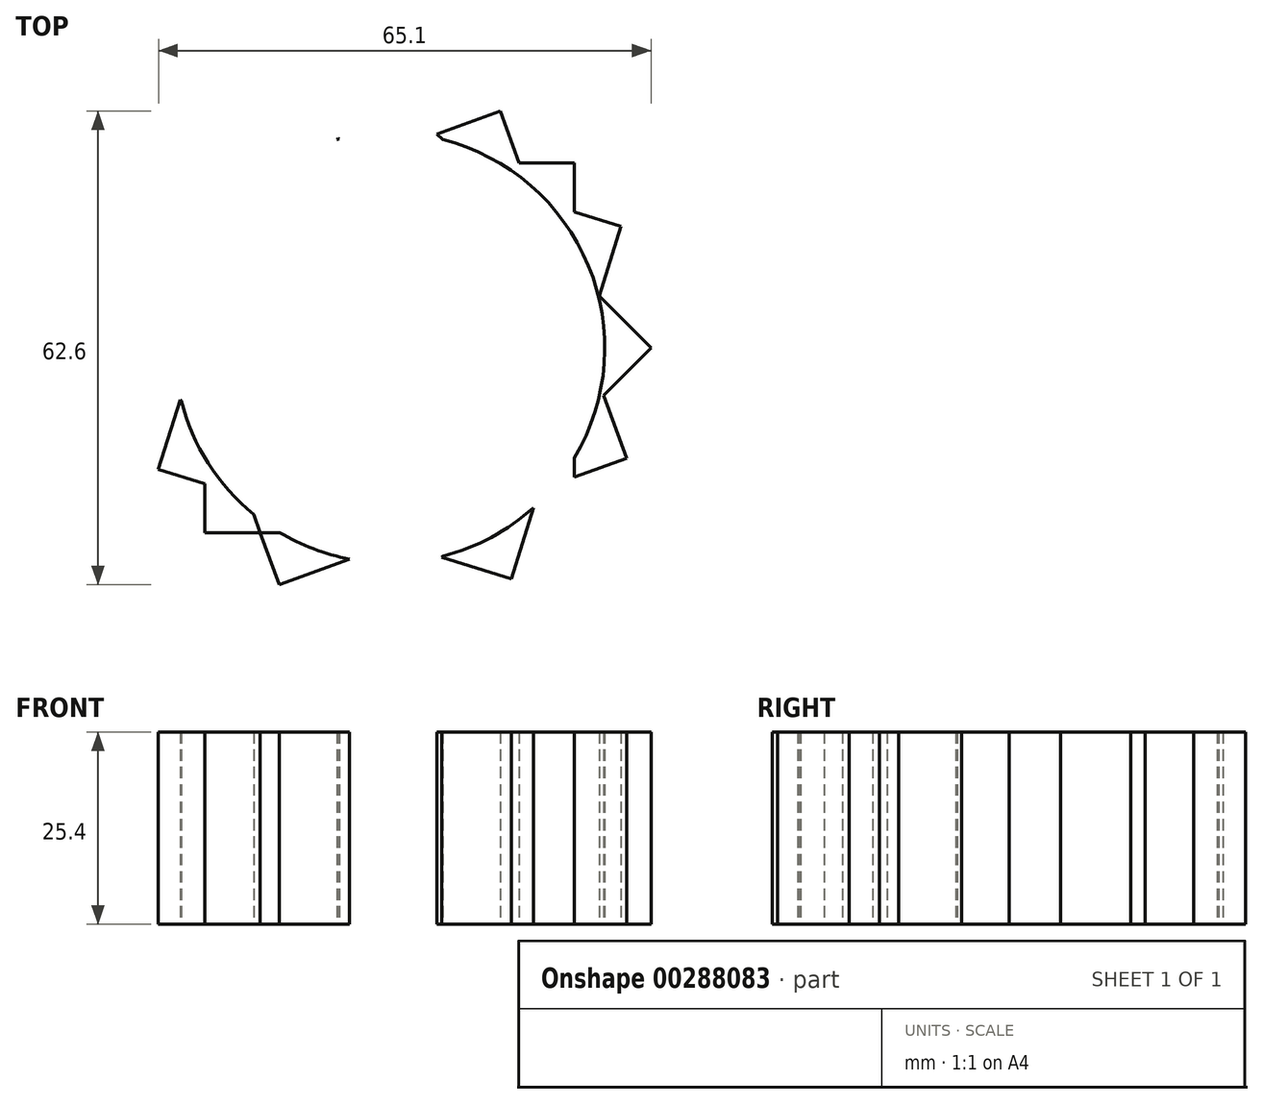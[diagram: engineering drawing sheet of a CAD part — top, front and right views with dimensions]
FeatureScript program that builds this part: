
annotation { "Feature Type Name" : "Feature", "Feature Type Description" : "" }
export const myFeature = defineFeature(function(context is Context, id is Id, definition is map)
    precondition{}
    {
        {
            var Q0;
            Q0=qCreatedBy(makeId("Top.planeOp"),FACE);
            var sketch = newSketch(context, id + "F0", { "sketchPlane" : qUnion([Q0])});
            skCircle(sketch, "E0", {"center": v(0, 0) * mm, "radius": 28.42 * mm});
            skLineSegment(sketch, "E1.bottom", {"start": v(24.42, -24.42) * mm, "end": v(14.53, -24.42) * mm});
            skLineSegment(sketch, "E1.top", {"start": v(34.54, 0) * mm, "end": v(27.54, 7) * mm});
            skLineSegment(sketch, "E1.left", {"start": v(24.42, -24.42) * mm, "end": v(24.42, -17.1) * mm});
            skLineSegment(sketch, "E2.MirrorCS", {"start": v(-24.42, 24.42) * mm, "end": v(-24.42, 17.1) * mm});
            skArc(sketch, "E3.MirrorC", {"start": v(0, 28.42) * mm, "mid": v(-3.52, -28.2) * mm, "end": v(7, 27.54) * mm});
            skLineSegment(sketch, "E4.MirrorCS", {"start": v(34.54, 0) * mm, "end": v(27.54, -7) * mm});
            skLineSegment(sketch, "E5.MirrorCS", {"start": v(-24.42, -24.42) * mm, "end": v(-24.42, -18) * mm});
            skLineSegment(sketch, "E6.MirrorCS", {"start": v(24.42, 24.42) * mm, "end": v(24.42, 18) * mm});
            skArc(sketch, "E7.MirrorC", {"start": v(-7, -27.54) * mm, "mid": v(3.52, 28.2) * mm, "end": v(0, -28.42) * mm});
            skLineSegment(sketch, "E8.MirrorCS", {"start": v(0, 34.54) * mm, "end": v(-7, 27.54) * mm});
            skLineSegment(sketch, "E9.MirrorCS", {"start": v(-24.42, -24.42) * mm, "end": v(-24.42, -14.53) * mm});
            skLineSegment(sketch, "E10.MirrorCS", {"start": v(0, -34.54) * mm, "end": v(-7, -27.54) * mm});
            skArc(sketch, "E11.MirrorC", {"start": v(-17.98, -22) * mm, "mid": v(28.4, 0.68) * mm, "end": v(-19.02, 21.12) * mm});
            skArc(sketch, "E12.MirrorC", {"start": v(7, 27.54) * mm, "mid": v(0, -28.42) * mm, "end": v(-7, 27.54) * mm});
            skLineSegment(sketch, "E13", {"start": v(24.42, 24.42) * mm, "end": v(17.1, 24.42) * mm});
            skPoint(sketch, "E14.orphan", {"position": v(28.42, 0) * mm});
            skPoint(sketch, "E15.MirrorCS.start.orphan", {"position": v(0, -28.42) * mm});
            skLineSegment(sketch, "E16.trimOffspring", {"start": v(-24.42, 17.1) * mm, "end": v(-24.42, 24.42) * mm});
            skPoint(sketch, "E17.MirrorCS.start.orphan", {"position": v(-28.42, 0) * mm});
            skPoint(sketch, "E18.MirrorCS.start.orphan", {"position": v(0, 28.42) * mm});
            skLineSegment(sketch, "E19.trimOffspring", {"start": v(-27.54, 7) * mm, "end": v(-34.54, 0) * mm});
            skLineSegment(sketch, "E20.trimOffspring", {"start": v(24.42, -14.53) * mm, "end": v(24.42, -24.42) * mm});
            skLineSegment(sketch, "E21.trimOffspring", {"start": v(7, 27.54) * mm, "end": v(0, 34.54) * mm});
            skPoint(sketch, "E22.MirrorCS.start.orphan", {"position": v(24.42, -24.42) * mm});
            skLineSegment(sketch, "E23.trimOffspring", {"start": v(7, -27.54) * mm, "end": v(0, -34.54) * mm});
            skLineSegment(sketch, "E24.trimOffspring", {"start": v(24.42, 18) * mm, "end": v(24.42, 24.42) * mm});
            skLineSegment(sketch, "E25.trimOffspring", {"start": v(24.42, -17.1) * mm, "end": v(24.42, -24.42) * mm});
            skPoint(sketch, "E26.MirrorCS.start.orphan", {"position": v(24.42, 24.42) * mm});
            skLineSegment(sketch, "E27.trimOffspring", {"start": v(-5.3, -27.92) * mm, "end": v(-14.6, -31.3) * mm});
            skLineSegment(sketch, "E28.trimOffspring", {"start": v(-27.54, -7) * mm, "end": v(-34.54, 0) * mm});
            skPoint(sketch, "E29.trimOffspring.end.orphan", {"position": v(-24.42, 24.42) * mm});
            skLineSegment(sketch, "E30.trimOffspring", {"start": v(-14.53, -24.42) * mm, "end": v(-24.42, -24.42) * mm});
            skLineSegment(sketch, "E31.trimOffspring", {"start": v(-27.92, 5.3) * mm, "end": v(-31.3, 14.6) * mm});
            skPoint(sketch, "E32.trimOffspring.end.orphan", {"position": v(-24.42, -24.42) * mm});
            skLineSegment(sketch, "E33.bottom", {"start": v(31.3, -14.6) * mm, "end": v(27.92, -5.3) * mm});
            skLineSegment(sketch, "E33.top", {"start": v(-14.6, -31.3) * mm, "end": v(-17.98, -22) * mm});
            skLineSegment(sketch, "E33.left", {"start": v(31.3, -14.6) * mm, "end": v(22, -17.98) * mm});
            skLineSegment(sketch, "E33.right", {"start": v(14.6, 31.3) * mm, "end": v(5.3, 27.92) * mm});
            skLineSegment(sketch, "E34.bottom", {"start": v(16.08, -30.56) * mm, "end": v(19.02, -21.12) * mm});
            skLineSegment(sketch, "E34.top", {"start": v(-30.56, -16.08) * mm, "end": v(-27.63, -6.64) * mm});
            skLineSegment(sketch, "E34.left", {"start": v(16.08, -30.56) * mm, "end": v(6.64, -27.63) * mm});
            skLineSegment(sketch, "E34.right", {"start": v(30.56, 16.08) * mm, "end": v(24.42, 18) * mm});
            skLineSegment(sketch, "E35.trimOffspring", {"start": v(-21.12, -19.02) * mm, "end": v(-30.56, -16.08) * mm});
            skLineSegment(sketch, "E36.trimOffspring", {"start": v(27.63, 6.64) * mm, "end": v(30.56, 16.08) * mm});
            skLineSegment(sketch, "E37.trimOffspring", {"start": v(17.1, 24.42) * mm, "end": v(14.6, 31.3) * mm});
            skLineSegment(sketch, "E38.trimOffspring", {"start": v(-6.64, 27.63) * mm, "end": v(-16.08, 30.56) * mm});
            skLineSegment(sketch, "E39.trimOffspring", {"start": v(-18, 24.42) * mm, "end": v(-16.08, 30.56) * mm});
            skLineSegment(sketch, "E40.trimOffspring", {"start": v(-24.42, 17.1) * mm, "end": v(-31.3, 14.6) * mm});
            skArc(sketch, "E41.trimOffspring", {"start": v(-22, 17.98) * mm, "mid": v(-28.4, -0.68) * mm, "end": v(-21.12, -19.02) * mm});
            skLineSegment(sketch, "E42", {"start": v(-24.42, 24.42) * mm, "end": v(-18, 24.42) * mm});
            skCircle(sketch, "E43", {"center": v(0, 0) * mm, "radius": 5.56 * mm});
            skSolve(sketch);
        }
        {
            var Q0;
            {var subQ3=sQuery(id+"F0.wireOp",EDGE,"E4.MirrorCS");var subQ7=sQuery(id+"F0.wireOp",EDGE,"E1.top");var subQ8=makeQuery(id+"F0.imprint","INTERSECT",VERTEX,{"derivedFrom":[subQ7,subQ3]});Q0=makeQuery(id+"F0.imprint","IMPRINT",FACE,{"disambiguationData":[TD([[makeQuery(id+"F0.imprint","IMPRINT",EDGE,{"disambiguationData":[TD([[subQ8,-1.0]])],"derivedFrom":subQ7}),1.0]])]});}
            var Q1;
            {var subQ0=sQuery(id+"F0.wireOp",EDGE,"E0");var subQ1=sQuery(id+"F0.wireOp",EDGE,"E1.top");var subQ2=makeQuery(id+"F0.imprint","INTERSECT",VERTEX,{"derivedFrom":[subQ1,subQ0]});Q1=makeQuery(id+"F0.imprint","IMPRINT",FACE,{"disambiguationData":[TD([[makeQuery(id+"F0.imprint","IMPRINT",EDGE,{"disambiguationData":[TD([[subQ2,1.0]])],"derivedFrom":subQ1}),1.0]])]});}
            var Q2;
            Q2=makeQuery(id+"F0.imprint","IMPRINT",FACE,{"disambiguationData":[TD([[makeQuery(id+"F0.imprint","IMPRINT",EDGE,{"derivedFrom":sQuery(id+"F0.wireOp",EDGE,"E13")}),1.0]])]});
            var Q3;
            {var subQ3=sQuery(id+"F0.wireOp",EDGE,"E4.MirrorCS");var subQ5=sQuery(id+"F0.wireOp",EDGE,"E0");var subQ6=makeQuery(id+"F0.imprint","INTERSECT",VERTEX,{"derivedFrom":[subQ3,subQ5]});Q3=makeQuery(id+"F0.imprint","IMPRINT",FACE,{"disambiguationData":[TD([[makeQuery(id+"F0.imprint","IMPRINT",EDGE,{"disambiguationData":[TD([[subQ6,1.0]])],"derivedFrom":subQ3}),1.0]])]});}
            var Q4;
            {var subQ0=sQuery(id+"F0.wireOp",EDGE,"E0");var subQ1=sQuery(id+"F0.wireOp",EDGE,"E4.MirrorCS");var subQ2=makeQuery(id+"F0.imprint","INTERSECT",VERTEX,{"derivedFrom":[subQ1,subQ0]});Q4=makeQuery(id+"F0.imprint","IMPRINT",FACE,{"disambiguationData":[TD([[makeQuery(id+"F0.imprint","IMPRINT",EDGE,{"disambiguationData":[TD([[subQ2,1.0]])],"derivedFrom":subQ1}),-1.0]])]});}
            var Q5;
            {var subQ3=sQuery(id+"F0.wireOp",EDGE,"E20.trimOffspring");var subQ5=sQuery(id+"F0.wireOp",EDGE,"E1.bottom");var subQ6=makeQuery(id+"F0.imprint","INTERSECT",VERTEX,{"derivedFrom":[subQ5,subQ3]});Q5=makeQuery(id+"F0.imprint","IMPRINT",FACE,{"disambiguationData":[TD([[makeQuery(id+"F0.imprint","IMPRINT",EDGE,{"disambiguationData":[TD([[subQ6,-1.0]])],"derivedFrom":subQ5}),-1.0]])]});}
            var Q6;
            {var subQ3=sQuery(id+"F0.wireOp",EDGE,"E1.bottom");var subQ5=sQuery(id+"F0.wireOp",EDGE,"E0");var subQ6=makeQuery(id+"F0.imprint","INTERSECT",VERTEX,{"derivedFrom":[subQ3,subQ5]});Q6=makeQuery(id+"F0.imprint","IMPRINT",FACE,{"disambiguationData":[TD([[makeQuery(id+"F0.imprint","IMPRINT",EDGE,{"disambiguationData":[TD([[subQ6,1.0]])],"derivedFrom":subQ3}),1.0]])]});}
            var Q7;
            {var subQ0=sQuery(id+"F0.wireOp",EDGE,"E0");var subQ1=sQuery(id+"F0.wireOp",EDGE,"E1.bottom");var subQ2=makeQuery(id+"F0.imprint","INTERSECT",VERTEX,{"derivedFrom":[subQ1,subQ0]});Q7=makeQuery(id+"F0.imprint","IMPRINT",FACE,{"disambiguationData":[TD([[makeQuery(id+"F0.imprint","IMPRINT",EDGE,{"disambiguationData":[TD([[subQ2,1.0]])],"derivedFrom":subQ1}),-1.0]])]});}
            var Q8;
            {var subQ6=sQuery(id+"F0.wireOp",EDGE,"E0");var subQ10=makeQuery(id+"F0.imprint","IMPRINT",VERTEX,{"disambiguationData":[OD(0.0)],"derivedFrom":subQ6});Q8=makeQuery(id+"F0.imprint","IMPRINT",FACE,{"disambiguationData":[TD([[makeQuery(id+"F0.imprint","IMPRINT",EDGE,{"disambiguationData":[TD([[subQ10,1.0]])],"derivedFrom":subQ6}),-1.0]])]});}
            var Q9;
            {var subQ0=sQuery(id+"F0.wireOp",EDGE,"E0");var subQ1=sQuery(id+"F0.wireOp",EDGE,"E8.MirrorCS");var subQ2=makeQuery(id+"F0.imprint","INTERSECT",VERTEX,{"derivedFrom":[subQ1,subQ0]});Q9=makeQuery(id+"F0.imprint","IMPRINT",FACE,{"disambiguationData":[TD([[makeQuery(id+"F0.imprint","IMPRINT",EDGE,{"disambiguationData":[TD([[subQ2,1.0]])],"derivedFrom":subQ1}),1.0]])]});}
            var Q10;
            Q10=makeQuery(id+"F0.imprint","IMPRINT",FACE,{"disambiguationData":[TD([[makeQuery(id+"F0.imprint","IMPRINT",EDGE,{"derivedFrom":sQuery(id+"F0.wireOp",EDGE,"E16.trimOffspring")}),-1.0]])]});
            var Q11;
            {var subQ7=sQuery(id+"F0.wireOp",EDGE,"E9.MirrorCS");Q11=makeQuery(id+"F0.imprint","IMPRINT",FACE,{"disambiguationData":[TD([[makeQuery(id+"F0.imprint","IMPRINT",EDGE,{"derivedFrom":subQ7}),1.0]])]});}
            var Q12;
            {var subQ0=sQuery(id+"F0.wireOp",EDGE,"E9.MirrorCS");Q12=makeQuery(id+"F0.imprint","IMPRINT",FACE,{"disambiguationData":[TD([[makeQuery(id+"F0.imprint","IMPRINT",EDGE,{"derivedFrom":subQ0}),-1.0]])]});}
            var Q13;
            {var subQ5=sQuery(id+"F0.wireOp",EDGE,"E5.MirrorCS");Q13=makeQuery(id+"F0.imprint","IMPRINT",FACE,{"disambiguationData":[TD([[makeQuery(id+"F0.imprint","IMPRINT",EDGE,{"derivedFrom":subQ5}),-1.0]])]});}
            var Q14;
            {var subQ5=sQuery(id+"F0.wireOp",EDGE,"E0");var subQ7=makeQuery(id+"F0.imprint","IMPRINT",VERTEX,{"disambiguationData":[OD(3.0)],"derivedFrom":subQ5});Q14=makeQuery(id+"F0.imprint","IMPRINT",FACE,{"disambiguationData":[TD([[makeQuery(id+"F0.imprint","IMPRINT",EDGE,{"disambiguationData":[TD([[subQ7,1.0]])],"derivedFrom":subQ5}),-1.0]])]});}
            var Q15;
            {var subQ5=sQuery(id+"F0.wireOp",EDGE,"E0");var subQ7=sQuery(id+"F0.wireOp",EDGE,"E10.MirrorCS");var subQ8=makeQuery(id+"F0.imprint","INTERSECT",VERTEX,{"derivedFrom":[subQ7,subQ5]});Q15=makeQuery(id+"F0.imprint","IMPRINT",FACE,{"disambiguationData":[TD([[makeQuery(id+"F0.imprint","IMPRINT",EDGE,{"disambiguationData":[TD([[subQ8,1.0]])],"derivedFrom":subQ7}),1.0]])]});}
            var Q16;
            {var subQ0=sQuery(id+"F0.wireOp",EDGE,"E0");var subQ1=sQuery(id+"F0.wireOp",EDGE,"E10.MirrorCS");var subQ2=makeQuery(id+"F0.imprint","INTERSECT",VERTEX,{"derivedFrom":[subQ1,subQ0]});Q16=makeQuery(id+"F0.imprint","IMPRINT",FACE,{"disambiguationData":[TD([[makeQuery(id+"F0.imprint","IMPRINT",EDGE,{"disambiguationData":[TD([[subQ2,1.0]])],"derivedFrom":subQ1}),-1.0]])]});}
            var Q17;
            {var subQ0=sQuery(id+"F0.wireOp",EDGE,"E21.trimOffspring");var subQ1=sQuery(id+"F0.wireOp",EDGE,"E0");var subQ2=makeQuery(id+"F0.imprint","INTERSECT",VERTEX,{"derivedFrom":[subQ1,subQ0]});Q17=makeQuery(id+"F0.imprint","IMPRINT",FACE,{"disambiguationData":[TD([[makeQuery(id+"F0.imprint","IMPRINT",EDGE,{"disambiguationData":[TD([[subQ2,-1.0]])],"derivedFrom":subQ1}),-1.0]])]});}
            var Q18;
            {var subQ0=sQuery(id+"F0.wireOp",EDGE,"E19.trimOffspring");var subQ1=sQuery(id+"F0.wireOp",EDGE,"E0");var subQ2=makeQuery(id+"F0.imprint","INTERSECT",VERTEX,{"derivedFrom":[subQ1,subQ0]});Q18=makeQuery(id+"F0.imprint","IMPRINT",FACE,{"disambiguationData":[TD([[makeQuery(id+"F0.imprint","IMPRINT",EDGE,{"disambiguationData":[TD([[subQ2,-1.0]])],"derivedFrom":subQ1}),-1.0]])]});}
            var Q19;
            {var subQ0=sQuery(id+"F0.wireOp",EDGE,"E34.top");var subQ1=sQuery(id+"F0.wireOp",EDGE,"E0");var subQ2=makeQuery(id+"F0.imprint","INTERSECT",VERTEX,{"derivedFrom":[subQ1,subQ0]});Q19=makeQuery(id+"F0.imprint","IMPRINT",FACE,{"disambiguationData":[TD([[makeQuery(id+"F0.imprint","IMPRINT",EDGE,{"disambiguationData":[TD([[subQ2,1.0]])],"derivedFrom":subQ1}),-1.0]])]});}
            var Q20;
            {var subQ0=sQuery(id+"F0.wireOp",EDGE,"E28.trimOffspring");var subQ1=sQuery(id+"F0.wireOp",EDGE,"E0");var subQ2=makeQuery(id+"F0.imprint","INTERSECT",VERTEX,{"derivedFrom":[subQ1,subQ0]});Q20=makeQuery(id+"F0.imprint","IMPRINT",FACE,{"disambiguationData":[TD([[makeQuery(id+"F0.imprint","IMPRINT",EDGE,{"disambiguationData":[TD([[subQ2,1.0]])],"derivedFrom":subQ1}),-1.0]])]});}
            var Q21;
            {var subQ0=sQuery(id+"F0.wireOp",EDGE,"E30.trimOffspring");var subQ1=sQuery(id+"F0.wireOp",EDGE,"E0");var subQ2=makeQuery(id+"F0.imprint","INTERSECT",VERTEX,{"derivedFrom":[subQ1,subQ0]});Q21=makeQuery(id+"F0.imprint","IMPRINT",FACE,{"disambiguationData":[TD([[makeQuery(id+"F0.imprint","IMPRINT",EDGE,{"disambiguationData":[TD([[subQ2,1.0]])],"derivedFrom":subQ1}),-1.0]])]});}
            var Q22;
            {var subQ0=sQuery(id+"F0.wireOp",EDGE,"E23.trimOffspring");var subQ1=sQuery(id+"F0.wireOp",EDGE,"E0");var subQ2=makeQuery(id+"F0.imprint","INTERSECT",VERTEX,{"derivedFrom":[subQ1,subQ0]});Q22=makeQuery(id+"F0.imprint","IMPRINT",FACE,{"disambiguationData":[TD([[makeQuery(id+"F0.imprint","IMPRINT",EDGE,{"disambiguationData":[TD([[subQ2,1.0]])],"derivedFrom":subQ1}),-1.0]])]});}
            var Q23;
            {var subQ0=sQuery(id+"F0.wireOp",EDGE,"E20.trimOffspring");var subQ1=sQuery(id+"F0.wireOp",EDGE,"E0");var subQ2=makeQuery(id+"F0.imprint","INTERSECT",VERTEX,{"derivedFrom":[subQ1,subQ0]});Q23=makeQuery(id+"F0.imprint","IMPRINT",FACE,{"disambiguationData":[TD([[makeQuery(id+"F0.imprint","IMPRINT",EDGE,{"disambiguationData":[TD([[subQ2,1.0]])],"derivedFrom":subQ1}),-1.0]])]});}
            var Q24;
            {var subQ0=sQuery(id+"F0.wireOp",EDGE,"E0");var subQ21=makeQuery(id+"F0.imprint","IMPRINT",VERTEX,{"disambiguationData":[OD(1.0)],"derivedFrom":subQ0});Q24=makeQuery(id+"F0.imprint","IMPRINT",FACE,{"disambiguationData":[TD([[makeQuery(id+"F0.imprint","IMPRINT",EDGE,{"disambiguationData":[TD([[subQ21,-1.0]])],"derivedFrom":subQ0}),1.0]])]});}
            extrude(context, id + "F1", {"entities" : qUnion([Q0, Q1, Q2, Q3, Q4, Q5, Q6, Q7, Q8, Q9, Q10, Q11, Q12, Q13, Q14, Q15, Q16, Q17, Q18, Q19, Q20, Q21, Q22, Q23, Q24]), "endBound" : BoundingType.SYMMETRIC, "depth" : 25.4 * mm});
        }
    });
